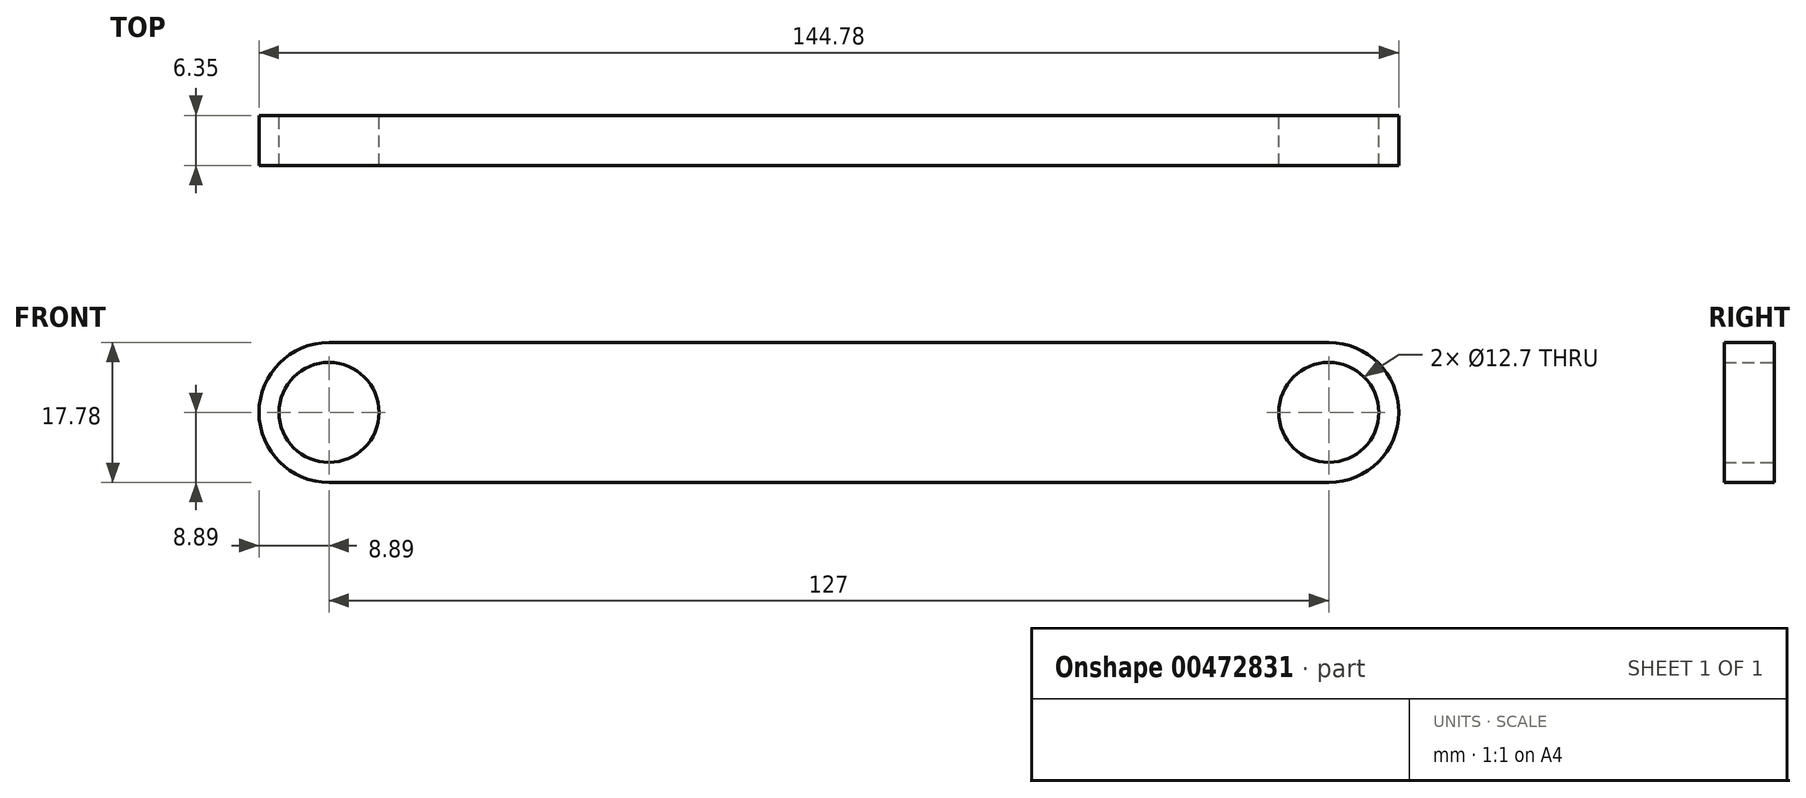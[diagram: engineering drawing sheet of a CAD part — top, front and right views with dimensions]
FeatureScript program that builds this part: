
annotation { "Feature Type Name" : "Feature", "Feature Type Description" : "" }
export const myFeature = defineFeature(function(context is Context, id is Id, definition is map)
    precondition{}
    {
        {
            var Q0;
            Q0=qCreatedBy(makeId("Front.planeOp"),FACE);
            var sketch = newSketch(context, id + "F0", { "sketchPlane" : qUnion([Q0])});
            skLineSegment(sketch, "E0.bottom", {"start": v(63.5, 8.9) * mm, "end": v(-63.5, 8.9) * mm});
            skLineSegment(sketch, "E0.top", {"start": v(63.5, -8.9) * mm, "end": v(-63.5, -8.9) * mm});
            skPoint(sketch, "E0.middle", {"position": v(0, 0) * mm});
            skArc(sketch, "E1", {"start": v(63.5, -8.9) * mm, "mid": v(72.4, 0) * mm, "end": v(63.5, 8.9) * mm});
            skArc(sketch, "E2.MirrorCS", {"start": v(-63.5, -8.9) * mm, "mid": v(-72.4, 0) * mm, "end": v(-63.5, 8.9) * mm});
            skCircle(sketch, "E3", {"center": v(-63.5, 0) * mm, "radius": 6.35 * mm});
            skCircle(sketch, "E4.MirrorC", {"center": v(63.5, 0) * mm, "radius": 6.35 * mm});
            skSolve(sketch);
        }
        {
            var Q0;
            Q0 = qSketchRegion(id + "F0", true);
            extrude(context, id + "F1", {"entities" : qUnion([Q0]), "depth" : 6.35 * mm});
        }
    });
